# Revit family: HVAC_Solar-Panels_HAJDU_HAJDU-M5-210_
name_source: partatom
category: Specialty Equipment
units: mm (PartAtom-declared; Revit-internal decimal feet)

## family parameters
Always vertical = No
Cut with Voids When Loaded = No
Maintain Annotation Orientation = No
OmniClass Number = 23.33.53.15
OmniClass Title = Solar Water Heating Collector Units
Part Type = Normal
Room Calculation Point = No
Round Connector Dimension = Use Diameter
Shared = No
Work Plane-Based = Yes

## types (1)
- M5-210
    Abszorbciós tényezo = a>0.95
    Anyaga = Szelektívbevonatú alumínium lemez 0.5 mm és rézcső D=0,8 mm
    Bevonat = szelektív
    Bruttó felület = 2.09 m2
    Burkolat (keret/hátlap) = eloxált alumínium
    Default Elevation = 1219.2 mm  [stored 4 ft]
    Description = A hajdu síkkollektorok több évtizedes élettartamukkal hosszútávon biztosítják a megfelelő működést. Szélsőséges időjárási körülményeknek is ellenáll az edzett- vagy speciális polimer anyaggal bevont szolár üvegeinek köszönhetően. Túlmelegedésre kevésbé érzékeny technológia, mivel nyáron esténként a vezérlés visszaforgatja a melegvizet, ezáltal visszahűti a rendszert. A kétévenkénti karbantartási igénye jóval kisebb, mint más technológiáknál. Monolit kialakításuk robusztus felépítést biztosít, korrózióvédelmet nyújt, kiküszöböli a hőhidakat valamint letisztult, modern megjelenést ad.
    Emissziós tényezo = e<0.035
    Felület = 1.99 m2
    Hatásfok tényezo a1 = 3.75 W/(m2K)
    Hatásfok tényezo a2 = 0.016 W/(m2K)
    Házház anyaga = Hajdu - Fém - Fekete
    Lefedés = 3.2 mm hőkezelt üveg
    Magasság = 1696 mm  [stored 5.5643 ft]
    Manufacturer = HAJDU
    Maximális hatásfok n0 = 0.78
    Maximális muködési homérséklet = 175.7 °C
    Maximális muködési nyomás = 1.0 MPa
    Model = M5-210
    Optikai hatásfok n0b = 0.795
    Product Page URL = https://hajdurt.hu
    Rádiusz = 11 mm  [stored 0.0360892 ft]
    Szigetelés anyaga = kőzetgyapot
    Szigetelés vastagság = 40 mm  [stored 0.131234 ft]
    Szélesség = 1230 mm  [stored 4.03543 ft]
    Tömeg = 42.00 kg
    Tömítés = EPDM
    URL = https://hajdurt.hu
    Vastagság = 86 mm  [stored 0.282152 ft]
    Vízcsatlakozás = 22 mm  [stored 0.0721785 ft]
    Üvegfelület (aperture) = 1.96 m2

note: [stored X ft] marks values corroborated as IEEE doubles in the binary element streams (Revit-internal decimal feet)

## geometry (parser evidence)
native form markers: Sweep x2
no freeform markers — native parametric forms only
